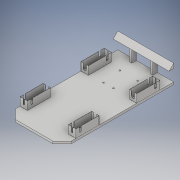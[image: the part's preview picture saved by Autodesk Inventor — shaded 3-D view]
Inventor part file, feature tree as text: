
AUTODESK INVENTOR PART (.ipt)
format: ipt  version: 2019 (Build 230136000, 136)  size: 344,064 bytes
history: native  units: in
note: dims shown in document units (in); Inventor stores cm internally (conversion verified against a paired STEP export)
features: reference x20, sketch x8, extrude x7, other x3, chamfer x2, plane x2, mirror x2, hole x1
ambient origin geometry x8: Origin, YZ Plane, XZ Plane, XY Plane, X Axis, Y Axis, Z Axis, Center Point
bodies: Solid1 (feature_tree)
feature tree (45):
  extrude  "Extrusion1"  Depth=12.0in
  extrude  "Extrusion2"  Depth=0.5in
  extrude  "Extrusion3"  TaperAngle=0.0deg  [1 undecoded]
  chamfer  "Chamfer1"  Distance=1.75in
  chamfer  "Chamfer2"  Distance=0.25in
  hole  "Hole1"  [1 undecoded]
  extrude  "Extrusion6"  Depth=1.75in
  extrude  "Extrusion7"  Depth=1.5in TaperAngle=0.0deg
  sketch  "Sketch14"  dims[d18=1.25in]
  plane  "Work Plane1"
  plane  "Work Plane2"
  extrude  "Extrusion8"  Depth=0.5in TaperAngle=45.0deg
  extrude  "Extrusion9"  Depth=0.886in TaperAngle=45.0deg
  mirror  "Mirror2"
  mirror  "Mirror3"
  sketch  "Sketch1"  dims[d0=6.0in d1=12.0in]
  sketch  "Sketch3"  dims[d2=2.0in d3=0.0in d8=0.5in]
  sketch  "Sketch4"  dims[d9=6.0in d10=0.0in]
  sketch  "Sketch8"  dims[d11=11.5in d12=1.75in d13=0.0in]
  sketch  "Sketch11"  dims[d15=1.75in]
  reference  "Reference5"
  reference  "Reference6"
  reference  "Reference7"
  reference  "Reference8"
  reference  "Reference9"
  reference  "Reference10"
  reference  "Reference11"
  reference  "Reference12"
  reference  "Reference13"
  reference  "Reference14"
  reference  "Reference15"
  reference  "Reference16"
  reference  "Reference17"
  reference  "Reference18"
  sketch  "Sketch13"  dims[d16=0.25in]
  reference  "Reference19"
  reference  "Reference20"
  reference  "Reference21"
  sketch  "Sketch15"  dims[d22=0.0in d23=0.25in d24=1.25in d25=1.75in d26=1.5in d27=0.0in d28=0.5in d29=0.125in d30=45.0deg d66=1.0in d67=0.125in d68=45.0deg d72=2.087in d73=2.648in d74=0.157in d75=0.115in d76=0.341in d77=0.157in d78=1.063in d79=0.157in d81=0.087in d84=0.157in d85=0.087in d87=0.959in d88=0.157in d89=0.75in d90=0.375in d91=0.25in d92=0.5635in d93=0.15in d94=0.8108in d99=2.004in d100=0.529in d101=0.529in d102=0.01in d103=0.01in d104=0.01in d105=0.01in d106=0.015in d107=0.015in d108=0.015in d109=0.886in d110=0.0in d111=90.0deg d112=90.0deg d113=0.886in d114=0.0in d115=3.0in d116=0.01in d118=90.0deg d119=0.886in d120=0.0in d121=0.01in d122=0.01in d123=0.886in d124=0.0in]
  reference  "Reference22"
  reference  "Reference23"
  reference  "Reference24"
  other  "<userpath>\Documents\Inventor\RC Car\RC Car Assembly.iam"
  other  "RC Car Assembly.iam"
  other  "Gear Motor:3"
note: 2 required parameter values undecoded (feature->parameter linkage not recoverable at this tier; creation-order binding heuristic only, values carry confidence <= 0.55)
